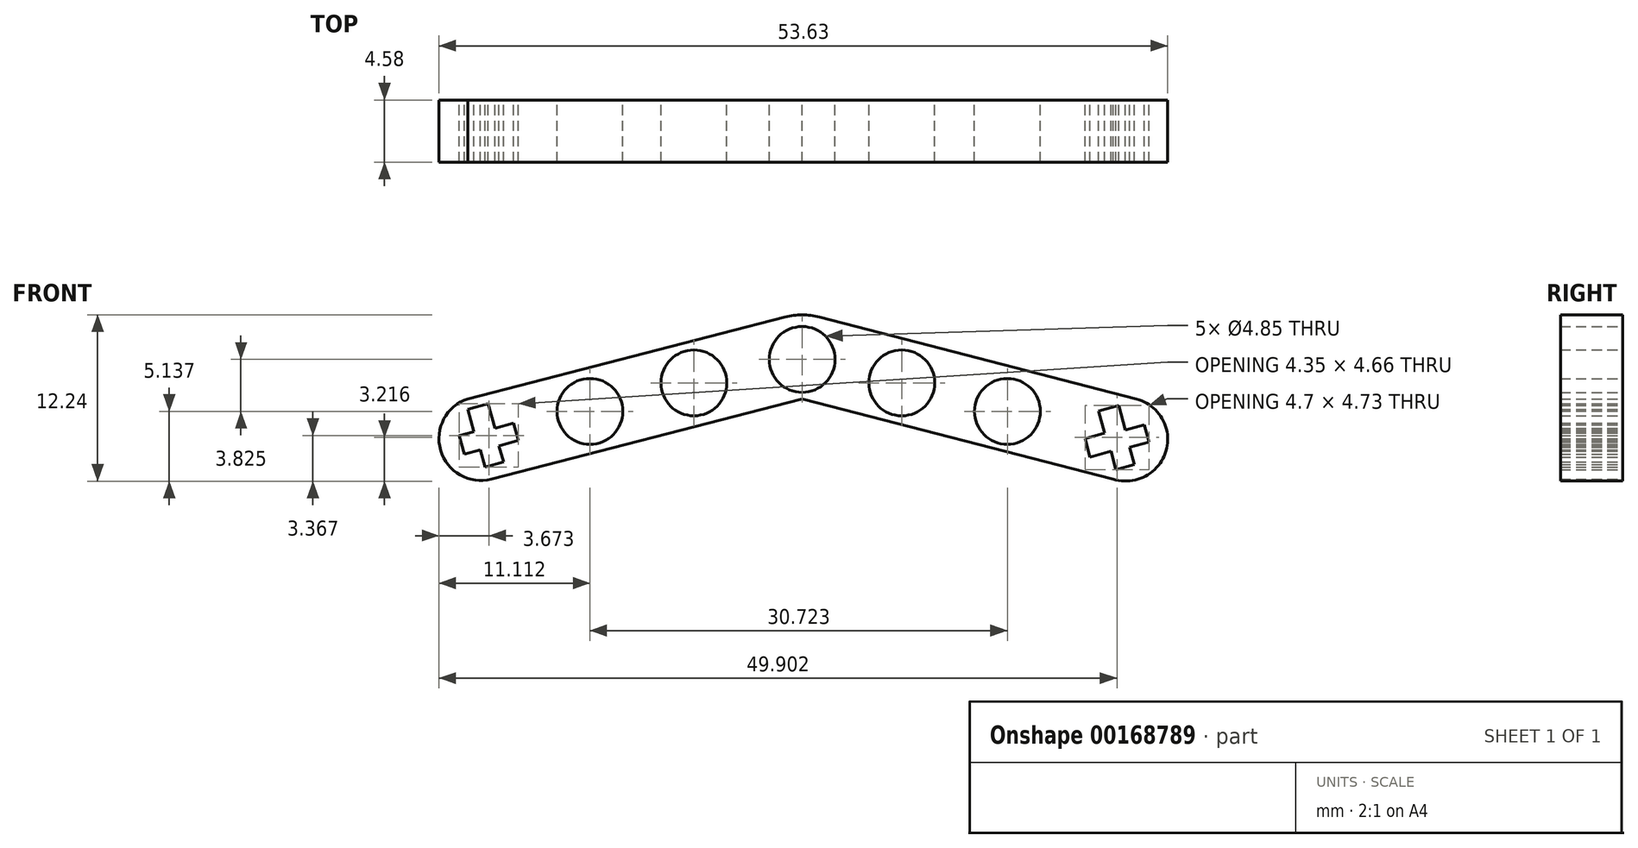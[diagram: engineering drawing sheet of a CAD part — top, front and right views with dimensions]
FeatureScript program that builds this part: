
annotation { "Feature Type Name" : "Feature", "Feature Type Description" : "" }
export const myFeature = defineFeature(function(context is Context, id is Id, definition is map)
    precondition{}
    {
        {
            var Q0;
            Q0=qCreatedBy(makeId("Front.planeOp"),FACE);
            var sketch = newSketch(context, id + "F0", { "sketchPlane" : qUnion([Q0])});
            skLineSegment(sketch, "E0", {"start": v(-24.6, 0) * mm, "end": v(0, 6.35) * mm});
            skLineSegment(sketch, "E1", {"start": v(0, 6.35) * mm, "end": v(24.6, 0) * mm});
            skLineSegment(sketch, "E2", {"start": v(0, 0) * mm, "end": v(-22.88, -5.9) * mm});
            skLineSegment(sketch, "E3", {"start": v(0, 0) * mm, "end": v(22.88, -5.9) * mm});
            skArc(sketch, "E4", {"start": v(-24.6, 0) * mm, "mid": v(-26.6, -3.79) * mm, "end": v(-22.88, -5.9) * mm});
            skArc(sketch, "E5", {"start": v(22.88, -5.9) * mm, "mid": v(26.78, -3.84) * mm, "end": v(24.6, 0) * mm});
            skLineSegment(sketch, "E6", {"start": v(-24.15, -2.41) * mm, "end": v(-24.6, -0.77) * mm});
            skLineSegment(sketch, "E7", {"start": v(-24.6, -0.77) * mm, "end": v(-23.1, -0.36) * mm});
            skLineSegment(sketch, "E8", {"start": v(-23.1, -0.36) * mm, "end": v(-22.6, -2.17) * mm});
            skLineSegment(sketch, "E9", {"start": v(-22.6, -2.17) * mm, "end": v(-21.23, -1.8) * mm});
            skLineSegment(sketch, "E10", {"start": v(-21.23, -1.8) * mm, "end": v(-20.88, -3.07) * mm});
            skLineSegment(sketch, "E11", {"start": v(-20.88, -3.07) * mm, "end": v(-22.3, -3.45) * mm});
            skLineSegment(sketch, "E12", {"start": v(-22.3, -3.45) * mm, "end": v(-21.98, -4.66) * mm});
            skLineSegment(sketch, "E13", {"start": v(-21.98, -4.66) * mm, "end": v(-23.34, -5.02) * mm});
            skLineSegment(sketch, "E14", {"start": v(-23.34, -5.02) * mm, "end": v(-23.68, -3.75) * mm});
            skLineSegment(sketch, "E15", {"start": v(-24.15, -2.41) * mm, "end": v(-25.23, -2.7) * mm});
            skLineSegment(sketch, "E16", {"start": v(-25.23, -2.7) * mm, "end": v(-24.86, -4.08) * mm});
            skLineSegment(sketch, "E17", {"start": v(-24.86, -4.08) * mm, "end": v(-23.68, -3.75) * mm});
            skLineSegment(sketch, "E18", {"start": v(22.25, -2.53) * mm, "end": v(21.8, -0.88) * mm});
            skLineSegment(sketch, "E19", {"start": v(21.8, -0.88) * mm, "end": v(23.3, -0.48) * mm});
            skLineSegment(sketch, "E20", {"start": v(23.3, -0.48) * mm, "end": v(23.8, -2.28) * mm});
            skLineSegment(sketch, "E21", {"start": v(23.8, -2.28) * mm, "end": v(25.18, -1.91) * mm});
            skLineSegment(sketch, "E22", {"start": v(25.18, -1.91) * mm, "end": v(25.52, -3.19) * mm});
            skLineSegment(sketch, "E23", {"start": v(25.52, -3.19) * mm, "end": v(24.1, -3.57) * mm});
            skLineSegment(sketch, "E24", {"start": v(24.1, -3.57) * mm, "end": v(24.44, -4.85) * mm});
            skLineSegment(sketch, "E25", {"start": v(23.09, -5.21) * mm, "end": v(22.72, -3.86) * mm});
            skLineSegment(sketch, "E26", {"start": v(22.25, -2.53) * mm, "end": v(20.82, -2.92) * mm});
            skLineSegment(sketch, "E27", {"start": v(21.2, -4.3) * mm, "end": v(22.72, -3.86) * mm});
            skLineSegment(sketch, "E28", {"start": v(20.82, -2.92) * mm, "end": v(21.2, -4.3) * mm});
            skLineSegment(sketch, "E29", {"start": v(23.09, -5.21) * mm, "end": v(24.44, -4.85) * mm});
            skCircle(sketch, "E30", {"center": v(15.1, -0.92) * mm, "radius": 2.42 * mm});
            skCircle(sketch, "E31", {"center": v(7.33, 1.17) * mm, "radius": 2.42 * mm});
            skCircle(sketch, "E32", {"center": v(0, 2.9) * mm, "radius": 2.42 * mm});
            skCircle(sketch, "E33", {"center": v(-7.97, 1.17) * mm, "radius": 2.42 * mm});
            skCircle(sketch, "E34", {"center": v(-15.62, -0.92) * mm, "radius": 2.42 * mm});
            skSolve(sketch);
        }
        {
            var Q0;
            Q0 = qSketchRegion(id + "F0", true);
            extrude(context, id + "F1", {"entities" : qUnion([Q0]), "endBound" : BoundingType.SYMMETRIC, "depth" : 4.57 * mm});
        }
        {
            var Q0;
            Q0=makeQuery(id+"F1.opExtrude","SWEPT_EDGE",EDGE,{"disambiguationData":[OSD([sQuery(id+"F0.wireOp",EDGE,"E0"),sQuery(id+"F0.wireOp",EDGE,"E1")])]});
            fillet(context, id + "F2", {"entities" : qUnion([Q0]), "radius" : 5.08 * mm, "tangentPropagation" : true, "allowEdgeOverflow" : false});
        }
    });
